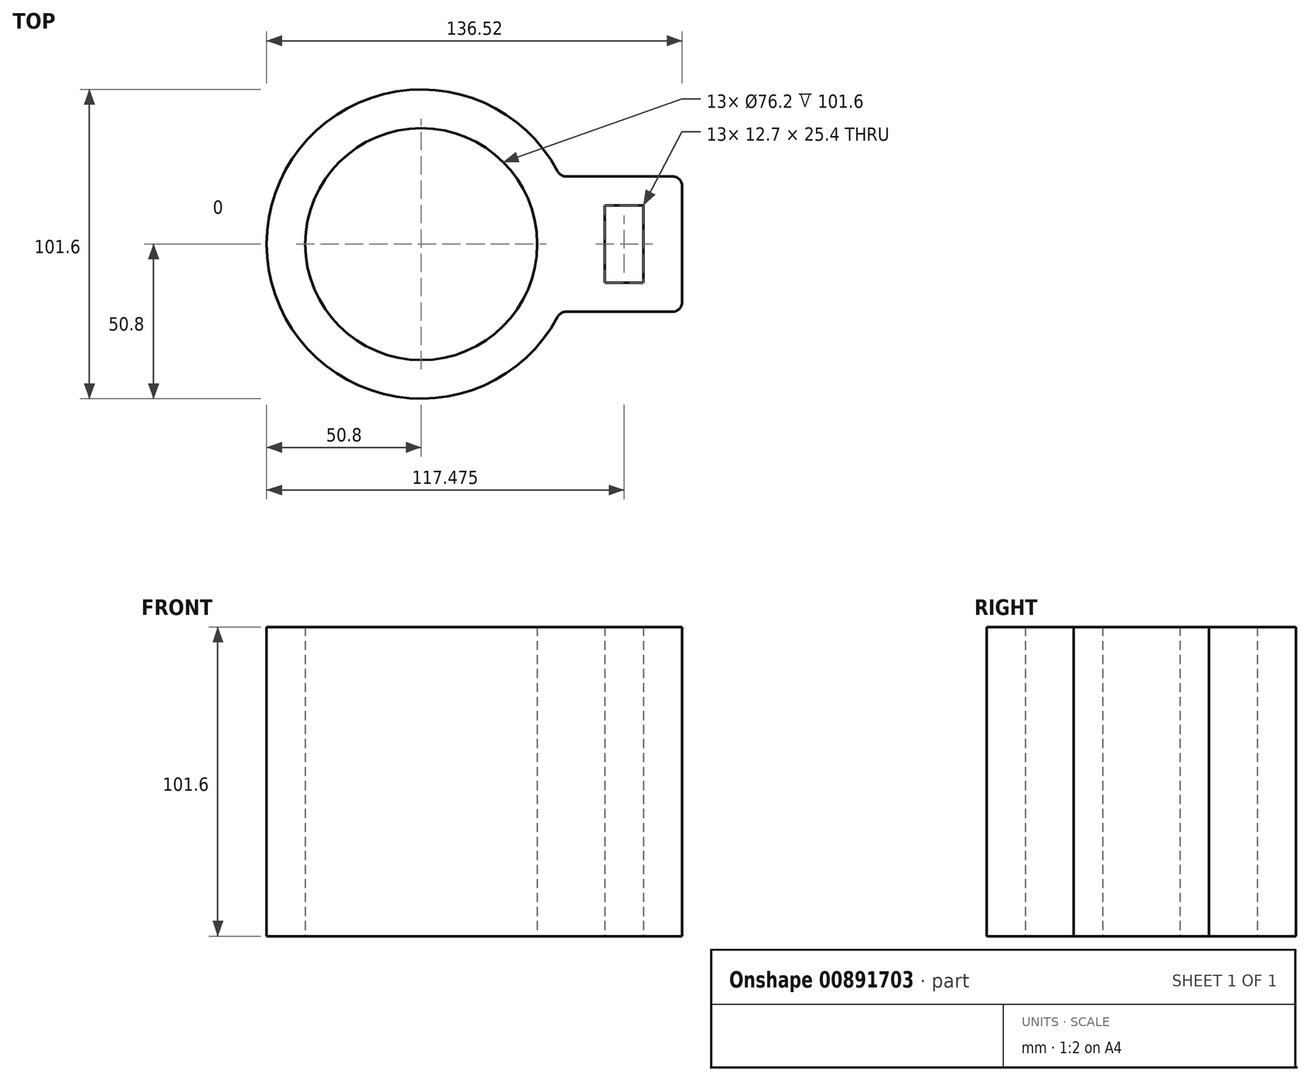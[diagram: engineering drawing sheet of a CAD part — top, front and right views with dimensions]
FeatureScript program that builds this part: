
annotation { "Feature Type Name" : "Feature", "Feature Type Description" : "" }
export const myFeature = defineFeature(function(context is Context, id is Id, definition is map)
    precondition{}
    {
        {
            var Q0;
            Q0=qCreatedBy(makeId("Top.planeOp"),FACE);
            var sketch = newSketch(context, id + "F0", { "sketchPlane" : qUnion([Q0])});
            skCircle(sketch, "E0", {"center": v(0, 0) * mm, "radius": 38.1 * mm});
            skLineSegment(sketch, "E1.bottom", {"start": v(60.33, 12.7) * mm, "end": v(73.03, 12.7) * mm});
            skLineSegment(sketch, "E1.top", {"start": v(60.33, -12.7) * mm, "end": v(73.03, -12.7) * mm});
            skLineSegment(sketch, "E1.left", {"start": v(60.33, 12.7) * mm, "end": v(60.33, -12.7) * mm});
            skLineSegment(sketch, "E1.right", {"start": v(73.03, 12.7) * mm, "end": v(73.03, -12.7) * mm});
            skPoint(sketch, "E1.middle", {"position": v(66.68, 0) * mm});
            skLineSegment(sketch, "E2.bottom", {"start": v(47.62, 22.23) * mm, "end": v(82.55, 22.23) * mm});
            skLineSegment(sketch, "E2.top", {"start": v(47.63, -22.22) * mm, "end": v(82.55, -22.22) * mm});
            skLineSegment(sketch, "E2.right", {"start": v(85.73, 19.05) * mm, "end": v(85.73, -19.05) * mm});
            skArc(sketch, "E3", {"start": v(44.82, 23.9) * mm, "mid": v(-50.8, 0) * mm, "end": v(44.82, -23.9) * mm});
            skArc(sketch, "E4", {"start": v(47.62, 22.23) * mm, "mid": v(46, 22.68) * mm, "end": v(44.82, 23.9) * mm});
            skArc(sketch, "E5", {"start": v(47.63, -22.22) * mm, "mid": v(46, -22.68) * mm, "end": v(44.82, -23.9) * mm});
            skPoint(sketch, "E6.visualSharp", {"position": v(85.73, 22.23) * mm});
            skArc(sketch, "E6.filletArc", {"start": v(85.73, 19.05) * mm, "mid": v(84.8, 21.3) * mm, "end": v(82.55, 22.23) * mm});
            skPoint(sketch, "E7.visualSharp", {"position": v(85.73, -22.22) * mm});
            skArc(sketch, "E7.filletArc", {"start": v(82.55, -22.22) * mm, "mid": v(84.8, -21.3) * mm, "end": v(85.73, -19.05) * mm});
            skSolve(sketch);
        }
        {
            var Q0;
            Q0 = qSketchRegion(id + "F0", true);
            extrude(context, id + "F1", {"entities" : qUnion([Q0]), "endBound" : BoundingType.SYMMETRIC, "depth" : 101.6 * mm, "offsetDistance" : 25.4 * mm});
        }
    });
